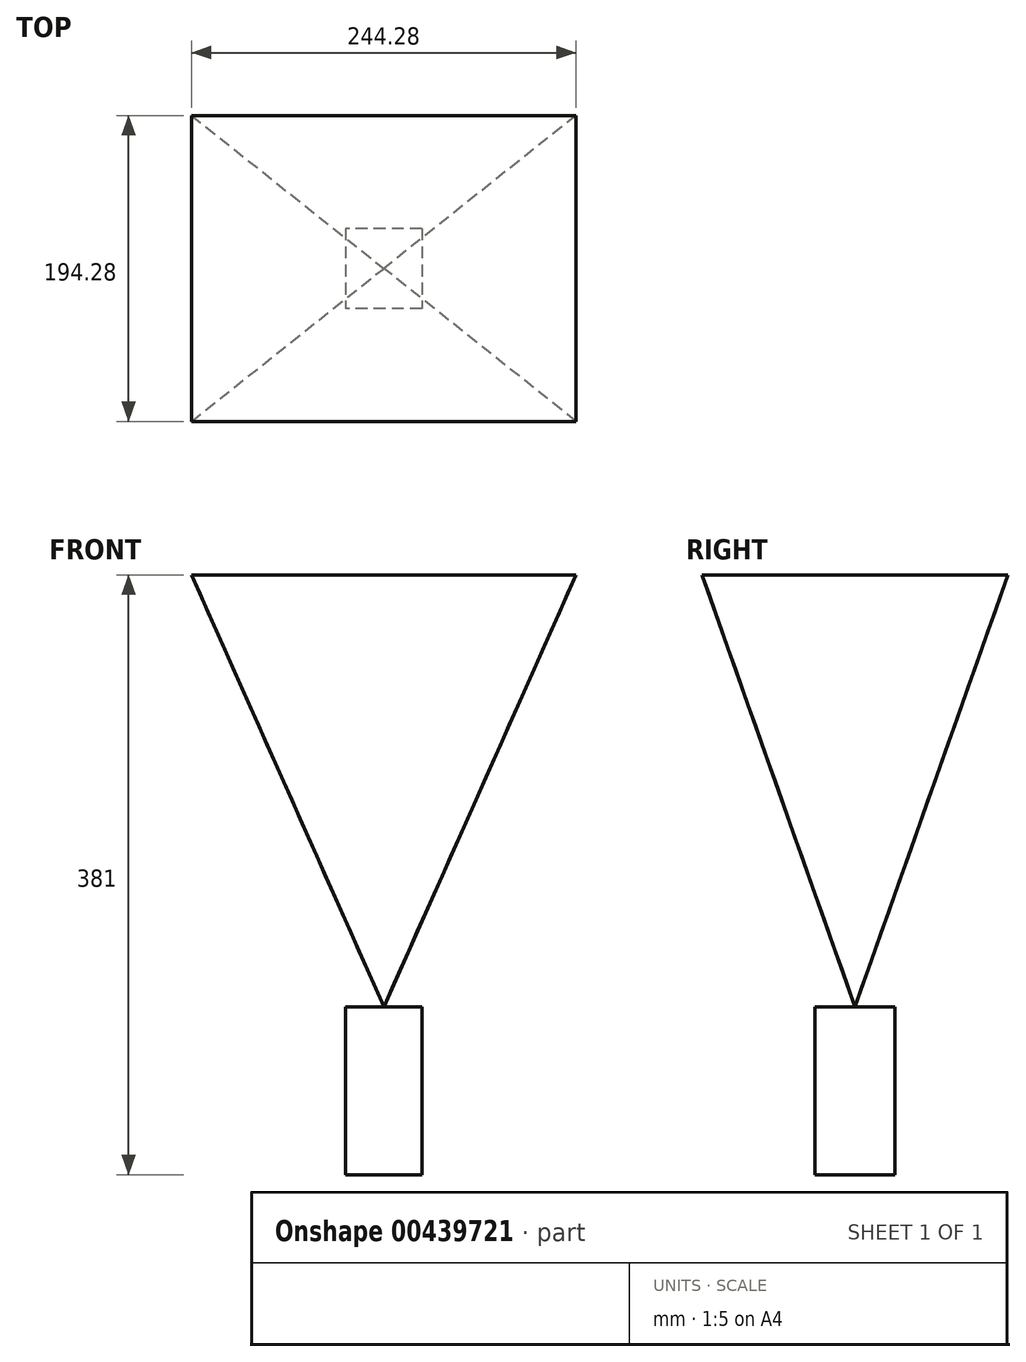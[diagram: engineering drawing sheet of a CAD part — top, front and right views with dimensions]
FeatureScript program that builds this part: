
annotation { "Feature Type Name" : "Feature", "Feature Type Description" : "" }
export const myFeature = defineFeature(function(context is Context, id is Id, definition is map)
    precondition{}
    {
        {
            var Q0;
            Q0=qCreatedBy(makeId("Top.planeOp"),FACE);
            var sketch = newSketch(context, id + "F0", { "sketchPlane" : qUnion([Q0])});
            skLineSegment(sketch, "E0.bottom", {"start": v(24.13, 25.4) * mm, "end": v(-24.13, 25.4) * mm});
            skLineSegment(sketch, "E0.top", {"start": v(24.13, -25.4) * mm, "end": v(-24.13, -25.4) * mm});
            skLineSegment(sketch, "E0.left", {"start": v(24.13, 25.4) * mm, "end": v(24.13, -25.4) * mm});
            skLineSegment(sketch, "E0.right", {"start": v(-24.13, 25.4) * mm, "end": v(-24.13, -25.4) * mm});
            skPoint(sketch, "E0.middle", {"position": v(0, 0) * mm});
            skSolve(sketch);
        }
        {
            var Q0;
            Q0 = qSketchRegion(id + "F0", true);
            extrude(context, id + "F1", {"entities" : qUnion([Q0]), "depth" : 106.68 * mm});
        }
        {
            var Q0;
            Q0=makeQuery(id+"F1.opExtrude","CAP_FACE",FACE,{"disambiguationData":[OSD([sQuery(id+"F0.wireOp",EDGE,"E0.bottom"),sQuery(id+"F0.wireOp",EDGE,"E0.top"),sQuery(id+"F0.wireOp",EDGE,"E0.left"),sQuery(id+"F0.wireOp",EDGE,"E0.right")])],"isStart":false});
            var sketch = newSketch(context, id + "F2", { "sketchPlane" : qUnion([Q0])});
            skLineSegment(sketch, "E1", {"start": v(-24.13, 0) * mm, "end": v(24.13, 0) * mm, "construction": true});
            skLineSegment(sketch, "E2", {"start": v(0, 25.4) * mm, "end": v(0, -25.4) * mm, "construction": true});
            skSolve(sketch);
        }
        {
            var Q0;
            Q0=qCreatedBy(makeId("Front.planeOp"),FACE);
            var sketch = newSketch(context, id + "F3", { "sketchPlane" : qUnion([Q0])});
            skPoint(sketch, "E3.0", {"position": v(0, 106.68) * mm});
            skLineSegment(sketch, "E4.0", {"start": v(-24.13, 106.68) * mm, "end": v(24.13, 106.68) * mm, "construction": true});
            skLineSegment(sketch, "E5", {"start": v(0, 106.68) * mm, "end": v(-101.98, 219.94) * mm, "construction": true});
            skLineSegment(sketch, "E6", {"start": v(0, 106.68) * mm, "end": v(0, 266.85) * mm, "construction": true});
            skLineSegment(sketch, "E7", {"start": v(0, 106.68) * mm, "end": v(61.99, 245.9) * mm});
            skSolve(sketch);
        }
        {
            var Q0;
            Q0=qCreatedBy(makeId("Right.planeOp"),FACE);
            var sketch = newSketch(context, id + "F4", { "sketchPlane" : qUnion([Q0])});
            skLineSegment(sketch, "E8.0", {"start": v(25.4, 106.68) * mm, "end": v(-25.4, 106.68) * mm, "construction": true});
            skPoint(sketch, "E8.1", {"position": v(0, 106.68) * mm});
            skLineSegment(sketch, "E9", {"start": v(0, 106.68) * mm, "end": v(59.35, 274.28) * mm});
            skLineSegment(sketch, "E10", {"start": v(0, 106.68) * mm, "end": v(-138.18, 218.57) * mm, "construction": true});
            skLineSegment(sketch, "E11", {"start": v(35.98, 208.28) * mm, "end": v(0, 208.28) * mm});
            skLineSegment(sketch, "E12", {"start": v(0, 208.28) * mm, "end": v(0, 106.68) * mm});
            skSolve(sketch);
        }
        {
            var Q0;
            Q0=qCreatedBy(makeId("Top.planeOp"),FACE);
            cPlane(context, id + "F5", {"entities" : qUnion([Q0]), "cplaneType" : CPlaneType.OFFSET, "offset" : 381 * mm, "width" : 152.4 * mm, "height" : 152.4 * mm});
        }
        {
            var Q0;
            Q0=qCreatedBy(id+"F5.planeOp",FACE);
            var sketch = newSketch(context, id + "F6", { "sketchPlane" : qUnion([Q0])});
            skPoint(sketch, "E13.2", {"position": v(0, 0) * mm});
            skPoint(sketch, "E14", {"position": v(0, 97.14) * mm});
            skPoint(sketch, "E15", {"position": v(122.14, 0) * mm});
            skLineSegment(sketch, "E16.bottom", {"start": v(-122.14, -97.14) * mm, "end": v(122.14, -97.14) * mm});
            skLineSegment(sketch, "E16.top", {"start": v(-122.14, 97.14) * mm, "end": v(122.14, 97.14) * mm});
            skLineSegment(sketch, "E16.left", {"start": v(-122.14, -97.14) * mm, "end": v(-122.14, 97.14) * mm});
            skLineSegment(sketch, "E16.right", {"start": v(122.14, -97.14) * mm, "end": v(122.14, 97.14) * mm});
            skSolve(sketch);
        }
        {
            var Q0;
            Q0=makeQuery(id+"F2.imprint","IMPRINT",FACE,{"disambiguationData":[TD([[makeQuery(id+"F2.imprint","IMPRINT",EDGE,{"derivedFrom":makeQuery(id+"F1.opExtrude","CAP_EDGE",EDGE,{"disambiguationData":[OSD([sQuery(id+"F0.wireOp",EDGE,"E0.bottom")])],"isStart":false})}),1.0]])]});
            var Q1;
            Q1=sQuery(id+"F4.wireOp",VERTEX,"E8.1");
            cPlane(context, id + "F7", {"entities" : qUnion([Q0, Q1]), "cplaneType" : CPlaneType.PLANE_POINT, "offset" : 25.4 * mm, "width" : 152.4 * mm, "height" : 152.4 * mm});
        }
        {
            var Q0;
            Q0=qCreatedBy(id+"F7.planeOp",FACE);
            var sketch = newSketch(context, id + "F8", { "sketchPlane" : qUnion([Q0])});
            skCircle(sketch, "E17", {"center": v(0, 0) * mm, "radius": 0 * mm});
            skSolve(sketch);
        }
        {
            var Q1;
            Q1 = qSketchRegion(id + "F6", true);
            var Q2;
            Q2 = qSketchRegion(id + "F8", true);
            loft(context, id + "F9", {"sheetProfilesArray" : [{ "sheetProfileEntities" : qUnion([Q1]) }, { "sheetProfileEntities" : qUnion([Q2]) }]});
        }
    });
